# Revit family: T-604CS_Ciclon CS
name_source: partatom
category: Plumbing Fixtures
revit_build: Autodesk Revit 2015 (Build: 20140606_1530(x64)
units: mm (PartAtom-declared; Revit-internal decimal feet)

## types (1)
- T-604 CICLON CS
    Apparent power = 200 VA
    Certificates = http://www.jimten.com
    Description = SANITARY MACERATOR FOR A BATHROOM, SIDE INLET
    Diameter Impulsion = 32 mm  [stored 0.104987 ft]
    Diameter Side inlet L = 40 mm  [stored 0.131234 ft]
    Diameter Side inlet R = 40 mm  [stored 0.131234 ft]
    Diameter Side intel T = 40 mm  [stored 0.131234 ft]
    Diameter WC = 100 mm  [stored 0.328084 ft]
    Flowrate = 1.7 L/s
    Inlets = 3 x Ø40 mm
    Load classification = Electrical appliances
    Manufacturer = Jimten
    Material = PP (Blanco)
    MaxPumping Height = 6 m vertical
    Model = T-604CS CICLON CS
    Network = 220-240 VAC 50HZ
    Number of poles = 1
    Outlet = 1 x Ø32mm
    Power = 470 W
    Reference = 75801
    Sanitary Appliance = No
    Type Comments = EASY MAINTENANCE THANKS TO ITS CASET SYSTEM. SILENT.
    U.Outlet Bidet-Shower = 2
    U.Outlet Wash basin = 1
    URL = http://www.jimten.com
    Voltage = 230 V
    WC = Yes
    WFU = 2

note: [stored X ft] marks values corroborated as IEEE doubles in the binary element streams (Revit-internal decimal feet)

## geometry (parser evidence)
native form markers: Blend x3, Sweep x1
no freeform markers — native parametric forms only
